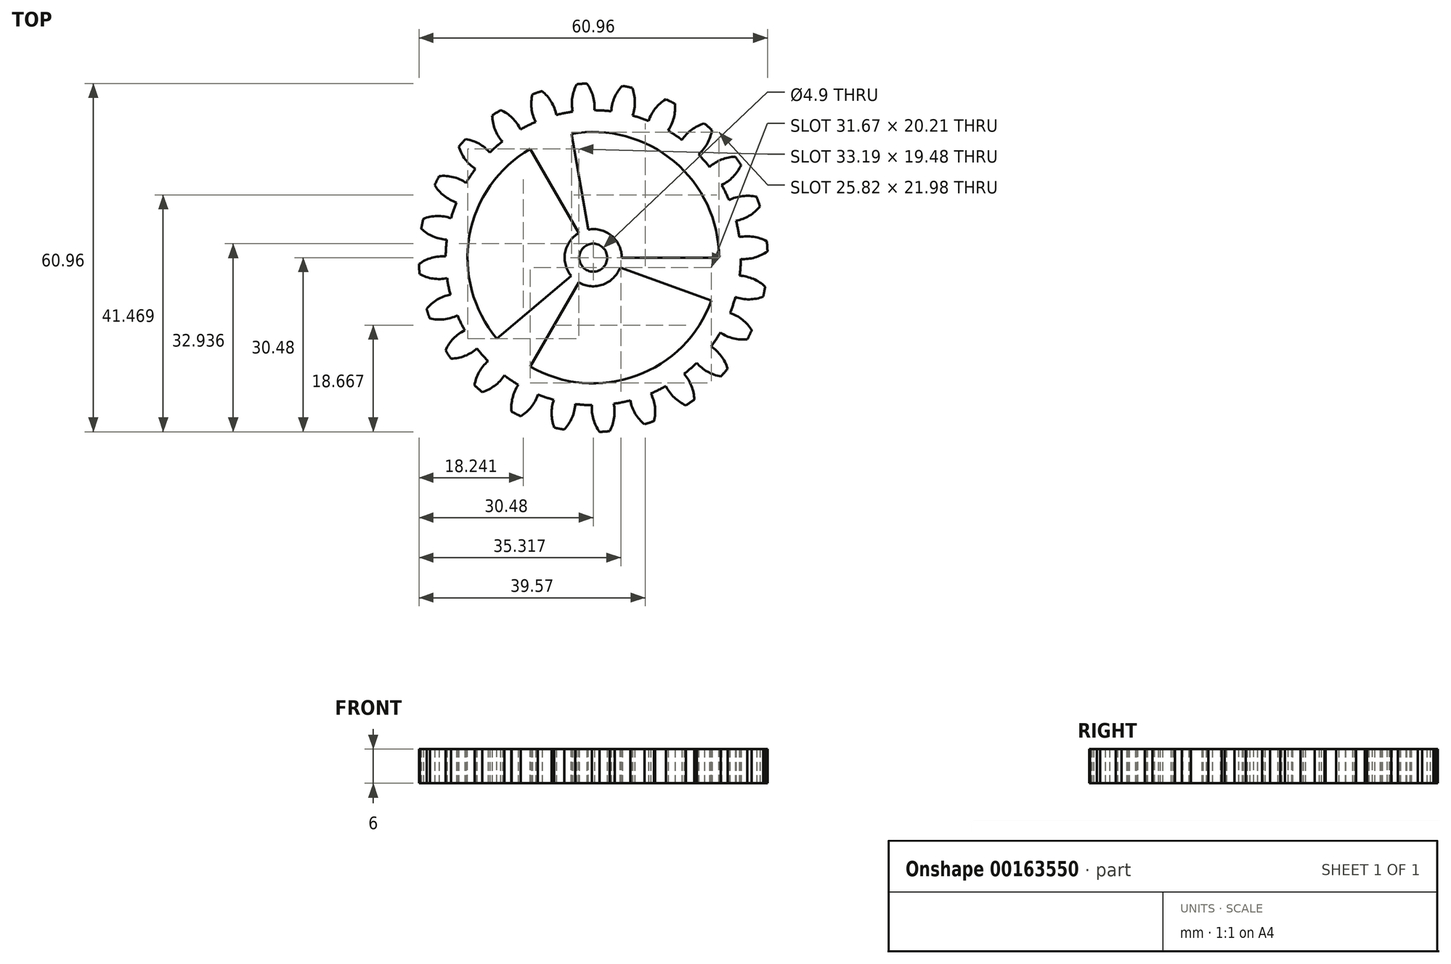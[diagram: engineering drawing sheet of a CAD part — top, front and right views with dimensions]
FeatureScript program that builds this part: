
annotation { "Feature Type Name" : "Feature", "Feature Type Description" : "" }
export const myFeature = defineFeature(function(context is Context, id is Id, definition is map)
    precondition{}
    {
        {
            var Q0;
            Q0=qCreatedBy(makeId("Top.planeOp"),FACE);
            var sketch = newSketch(context, id + "F0", { "sketchPlane" : qUnion([Q0])});
            skCircle(sketch, "E0", {"center": v(0, 0) * mm, "radius": 25.8 * mm, "construction": true});
            skCircle(sketch, "E1", {"center": v(0, 0) * mm, "radius": 28.15 * mm, "construction": true});
            skCircle(sketch, "E2", {"center": v(0, 0) * mm, "radius": 30.5 * mm, "construction": true});
            skLineSegment(sketch, "E3", {"start": v(0, 0) * mm, "end": v(0, 14.58) * mm, "construction": true});
            skLineSegment(sketch, "E4", {"start": v(0, 0) * mm, "end": v(-0.95, 14.56) * mm, "construction": true});
            skLineSegment(sketch, "E5", {"start": v(0, 28.15) * mm, "end": v(-10.54, 28.15) * mm, "construction": true});
            skLineSegment(sketch, "E6", {"start": v(0, 28.15) * mm, "end": v(-11.63, 25.04) * mm, "construction": true});
            skCircle(sketch, "E7", {"center": v(0, 28.15) * mm, "radius": 7.04 * mm, "construction": true});
            skCircle(sketch, "E8", {"center": v(-6.8, 26.33) * mm, "radius": 7.04 * mm, "construction": true});
            skArc(sketch, "E9", {"start": v(-13.6, 28.15) * mm, "mid": v(-13.7, 27.68) * mm, "end": v(-13.78, 27.2) * mm});
            skPoint(sketch, "E10.center", {"position": v(4.35, 4.65) * mm});
            skCircle(sketch, "E11", {"center": v(0, 0) * mm, "radius": 2.45 * mm});
            skArc(sketch, "E12", {"start": v(0.22, 25.8) * mm, "mid": v(-0.03, 28.26) * mm, "end": v(-1.11, 30.48) * mm});
            skArc(sketch, "E13.MirrorCS", {"start": v(-3.59, 25.56) * mm, "mid": v(-3.66, 28.02) * mm, "end": v(-2.88, 30.36) * mm});
            skArc(sketch, "E14", {"start": v(-1.11, 30.48) * mm, "mid": v(-2, 30.43) * mm, "end": v(-2.88, 30.36) * mm});
            skArc(sketch, "E15.1.0", {"start": v(-8.96, 29.15) * mm, "mid": v(-9.8, 28.88) * mm, "end": v(-10.64, 28.59) * mm});
            skArc(sketch, "E15.1.1", {"start": v(-6.47, 24.98) * mm, "mid": v(-7.34, 27.3) * mm, "end": v(-8.96, 29.15) * mm});
            skArc(sketch, "E15.1.2", {"start": v(-10.08, 23.76) * mm, "mid": v(-10.79, 26.12) * mm, "end": v(-10.64, 28.59) * mm});
            skArc(sketch, "E15.2.0", {"start": v(-16.2, 25.84) * mm, "mid": v(-16.94, 25.36) * mm, "end": v(-17.67, 24.86) * mm});
            skArc(sketch, "E15.2.1", {"start": v(-12.71, 22.46) * mm, "mid": v(-14.16, 24.46) * mm, "end": v(-16.2, 25.84) * mm});
            skArc(sketch, "E15.2.2", {"start": v(-15.88, 20.34) * mm, "mid": v(-17.18, 22.44) * mm, "end": v(-17.67, 24.86) * mm});
            skArc(sketch, "E15.3.0", {"start": v(-22.34, 20.77) * mm, "mid": v(-22.93, 20.11) * mm, "end": v(-23.5, 19.44) * mm});
            skArc(sketch, "E15.3.1", {"start": v(-18.1, 18.4) * mm, "mid": v(-20, 19.96) * mm, "end": v(-22.34, 20.77) * mm});
            skArc(sketch, "E15.3.2", {"start": v(-20.6, 15.54) * mm, "mid": v(-22.4, 17.23) * mm, "end": v(-23.5, 19.44) * mm});
            skArc(sketch, "E15.4.0", {"start": v(-26.95, 14.28) * mm, "mid": v(-27.35, 13.49) * mm, "end": v(-27.73, 12.7) * mm});
            skArc(sketch, "E15.4.1", {"start": v(-22.24, 13.1) * mm, "mid": v(-24.5, 14.1) * mm, "end": v(-26.95, 14.28) * mm});
            skArc(sketch, "E15.4.2", {"start": v(-23.93, 9.67) * mm, "mid": v(-26.1, 10.84) * mm, "end": v(-27.73, 12.7) * mm});
            skArc(sketch, "E15.5.0", {"start": v(-29.73, 6.81) * mm, "mid": v(-29.91, 5.95) * mm, "end": v(-30.07, 5.08) * mm});
            skArc(sketch, "E15.5.1", {"start": v(-24.87, 6.9) * mm, "mid": v(-27.3, 7.29) * mm, "end": v(-29.73, 6.81) * mm});
            skArc(sketch, "E15.5.2", {"start": v(-25.61, 3.15) * mm, "mid": v(-28.02, 3.72) * mm, "end": v(-30.07, 5.08) * mm});
            skArc(sketch, "E15.6.0", {"start": v(-30.48, -1.11) * mm, "mid": v(-30.43, -2) * mm, "end": v(-30.36, -2.88) * mm});
            skArc(sketch, "E15.6.1", {"start": v(-25.8, 0.22) * mm, "mid": v(-28.26, -0.03) * mm, "end": v(-30.48, -1.11) * mm});
            skArc(sketch, "E15.6.2", {"start": v(-25.56, -3.59) * mm, "mid": v(-28.02, -3.66) * mm, "end": v(-30.36, -2.88) * mm});
            skArc(sketch, "E15.7.0", {"start": v(-29.15, -8.96) * mm, "mid": v(-28.88, -9.8) * mm, "end": v(-28.59, -10.64) * mm});
            skArc(sketch, "E15.7.1", {"start": v(-24.98, -6.47) * mm, "mid": v(-27.3, -7.34) * mm, "end": v(-29.15, -8.96) * mm});
            skArc(sketch, "E15.7.2", {"start": v(-23.76, -10.08) * mm, "mid": v(-26.12, -10.79) * mm, "end": v(-28.59, -10.64) * mm});
            skArc(sketch, "E15.8.0", {"start": v(-25.84, -16.2) * mm, "mid": v(-25.36, -16.94) * mm, "end": v(-24.86, -17.67) * mm});
            skArc(sketch, "E15.8.1", {"start": v(-22.46, -12.71) * mm, "mid": v(-24.46, -14.16) * mm, "end": v(-25.84, -16.2) * mm});
            skArc(sketch, "E15.8.2", {"start": v(-20.34, -15.88) * mm, "mid": v(-22.44, -17.18) * mm, "end": v(-24.86, -17.67) * mm});
            skArc(sketch, "E15.9.0", {"start": v(-20.77, -22.34) * mm, "mid": v(-20.11, -22.93) * mm, "end": v(-19.44, -23.5) * mm});
            skArc(sketch, "E15.9.1", {"start": v(-18.4, -18.1) * mm, "mid": v(-19.96, -20) * mm, "end": v(-20.77, -22.34) * mm});
            skArc(sketch, "E15.9.2", {"start": v(-15.54, -20.6) * mm, "mid": v(-17.23, -22.4) * mm, "end": v(-19.44, -23.5) * mm});
            skArc(sketch, "E15.10.0", {"start": v(-14.28, -26.95) * mm, "mid": v(-13.49, -27.35) * mm, "end": v(-12.7, -27.73) * mm});
            skArc(sketch, "E15.10.1", {"start": v(-13.1, -22.24) * mm, "mid": v(-14.1, -24.5) * mm, "end": v(-14.28, -26.95) * mm});
            skArc(sketch, "E15.10.2", {"start": v(-9.67, -23.93) * mm, "mid": v(-10.84, -26.1) * mm, "end": v(-12.7, -27.73) * mm});
            skArc(sketch, "E15.11.0", {"start": v(-6.81, -29.73) * mm, "mid": v(-5.95, -29.91) * mm, "end": v(-5.08, -30.07) * mm});
            skArc(sketch, "E15.11.1", {"start": v(-6.9, -24.87) * mm, "mid": v(-7.29, -27.3) * mm, "end": v(-6.81, -29.73) * mm});
            skArc(sketch, "E15.11.2", {"start": v(-3.15, -25.61) * mm, "mid": v(-3.72, -28.02) * mm, "end": v(-5.08, -30.07) * mm});
            skArc(sketch, "E15.12.0", {"start": v(1.11, -30.48) * mm, "mid": v(2, -30.43) * mm, "end": v(2.88, -30.36) * mm});
            skArc(sketch, "E15.12.1", {"start": v(-0.22, -25.8) * mm, "mid": v(0.03, -28.26) * mm, "end": v(1.11, -30.48) * mm});
            skArc(sketch, "E15.12.2", {"start": v(3.59, -25.56) * mm, "mid": v(3.66, -28.02) * mm, "end": v(2.88, -30.36) * mm});
            skArc(sketch, "E15.13.0", {"start": v(8.96, -29.15) * mm, "mid": v(9.8, -28.88) * mm, "end": v(10.64, -28.59) * mm});
            skArc(sketch, "E15.13.1", {"start": v(6.47, -24.98) * mm, "mid": v(7.34, -27.3) * mm, "end": v(8.96, -29.15) * mm});
            skArc(sketch, "E15.13.2", {"start": v(10.08, -23.76) * mm, "mid": v(10.79, -26.12) * mm, "end": v(10.64, -28.59) * mm});
            skArc(sketch, "E15.14.0", {"start": v(16.2, -25.84) * mm, "mid": v(16.94, -25.36) * mm, "end": v(17.67, -24.86) * mm});
            skArc(sketch, "E15.14.1", {"start": v(12.71, -22.46) * mm, "mid": v(14.16, -24.46) * mm, "end": v(16.2, -25.84) * mm});
            skArc(sketch, "E15.14.2", {"start": v(15.88, -20.34) * mm, "mid": v(17.18, -22.44) * mm, "end": v(17.67, -24.86) * mm});
            skArc(sketch, "E15.15.0", {"start": v(22.34, -20.77) * mm, "mid": v(22.93, -20.11) * mm, "end": v(23.5, -19.44) * mm});
            skArc(sketch, "E15.15.1", {"start": v(18.1, -18.4) * mm, "mid": v(20, -19.96) * mm, "end": v(22.34, -20.77) * mm});
            skArc(sketch, "E15.15.2", {"start": v(20.6, -15.54) * mm, "mid": v(22.4, -17.23) * mm, "end": v(23.5, -19.44) * mm});
            skArc(sketch, "E15.16.0", {"start": v(26.95, -14.28) * mm, "mid": v(27.35, -13.49) * mm, "end": v(27.73, -12.7) * mm});
            skArc(sketch, "E15.16.1", {"start": v(22.24, -13.1) * mm, "mid": v(24.5, -14.1) * mm, "end": v(26.95, -14.28) * mm});
            skArc(sketch, "E15.16.2", {"start": v(23.93, -9.67) * mm, "mid": v(26.1, -10.84) * mm, "end": v(27.73, -12.7) * mm});
            skArc(sketch, "E15.17.0", {"start": v(29.73, -6.81) * mm, "mid": v(29.91, -5.95) * mm, "end": v(30.07, -5.08) * mm});
            skArc(sketch, "E15.17.1", {"start": v(24.87, -6.9) * mm, "mid": v(27.3, -7.29) * mm, "end": v(29.73, -6.81) * mm});
            skArc(sketch, "E15.17.2", {"start": v(25.61, -3.15) * mm, "mid": v(28.02, -3.72) * mm, "end": v(30.07, -5.08) * mm});
            skArc(sketch, "E15.18.0", {"start": v(30.48, 1.11) * mm, "mid": v(30.43, 2) * mm, "end": v(30.36, 2.88) * mm});
            skArc(sketch, "E15.18.1", {"start": v(25.8, -0.22) * mm, "mid": v(28.26, 0.03) * mm, "end": v(30.48, 1.11) * mm});
            skArc(sketch, "E15.18.2", {"start": v(25.56, 3.59) * mm, "mid": v(28.02, 3.66) * mm, "end": v(30.36, 2.88) * mm});
            skArc(sketch, "E15.19.0", {"start": v(29.15, 8.96) * mm, "mid": v(28.88, 9.8) * mm, "end": v(28.59, 10.64) * mm});
            skArc(sketch, "E15.19.1", {"start": v(24.98, 6.47) * mm, "mid": v(27.3, 7.34) * mm, "end": v(29.15, 8.96) * mm});
            skArc(sketch, "E15.19.2", {"start": v(23.76, 10.08) * mm, "mid": v(26.12, 10.79) * mm, "end": v(28.59, 10.64) * mm});
            skArc(sketch, "E15.20.0", {"start": v(25.84, 16.2) * mm, "mid": v(25.36, 16.94) * mm, "end": v(24.86, 17.67) * mm});
            skArc(sketch, "E15.20.1", {"start": v(22.46, 12.71) * mm, "mid": v(24.46, 14.16) * mm, "end": v(25.84, 16.2) * mm});
            skArc(sketch, "E15.20.2", {"start": v(20.34, 15.88) * mm, "mid": v(22.44, 17.18) * mm, "end": v(24.86, 17.67) * mm});
            skArc(sketch, "E15.21.0", {"start": v(20.77, 22.34) * mm, "mid": v(20.11, 22.93) * mm, "end": v(19.44, 23.5) * mm});
            skArc(sketch, "E15.21.1", {"start": v(18.4, 18.1) * mm, "mid": v(19.96, 20) * mm, "end": v(20.77, 22.34) * mm});
            skArc(sketch, "E15.21.2", {"start": v(15.54, 20.6) * mm, "mid": v(17.23, 22.4) * mm, "end": v(19.44, 23.5) * mm});
            skArc(sketch, "E15.22.0", {"start": v(14.28, 26.95) * mm, "mid": v(13.49, 27.35) * mm, "end": v(12.7, 27.73) * mm});
            skArc(sketch, "E15.22.1", {"start": v(13.1, 22.24) * mm, "mid": v(14.1, 24.5) * mm, "end": v(14.28, 26.95) * mm});
            skArc(sketch, "E15.22.2", {"start": v(9.67, 23.93) * mm, "mid": v(10.84, 26.1) * mm, "end": v(12.7, 27.73) * mm});
            skArc(sketch, "E15.23.0", {"start": v(6.81, 29.73) * mm, "mid": v(5.95, 29.91) * mm, "end": v(5.08, 30.07) * mm});
            skArc(sketch, "E15.23.1", {"start": v(6.9, 24.87) * mm, "mid": v(7.29, 27.3) * mm, "end": v(6.81, 29.73) * mm});
            skArc(sketch, "E15.23.2", {"start": v(3.15, 25.61) * mm, "mid": v(3.72, 28.02) * mm, "end": v(5.08, 30.07) * mm});
            skArc(sketch, "E16", {"start": v(3.15, 25.61) * mm, "mid": v(1.69, 25.75) * mm, "end": v(0.22, 25.8) * mm});
            skArc(sketch, "E17.1.0", {"start": v(-3.59, 25.56) * mm, "mid": v(-5.03, 25.31) * mm, "end": v(-6.47, 24.98) * mm});
            skArc(sketch, "E17.2.0", {"start": v(-10.08, 23.76) * mm, "mid": v(-11.41, 23.15) * mm, "end": v(-12.71, 22.46) * mm});
            skArc(sketch, "E17.3.0", {"start": v(-15.88, 20.34) * mm, "mid": v(-17.02, 19.4) * mm, "end": v(-18.1, 18.4) * mm});
            skArc(sketch, "E17.4.0", {"start": v(-20.6, 15.54) * mm, "mid": v(-21.46, 14.34) * mm, "end": v(-22.24, 13.1) * mm});
            skArc(sketch, "E17.5.0", {"start": v(-23.93, 9.67) * mm, "mid": v(-24.44, 8.3) * mm, "end": v(-24.87, 6.9) * mm});
            skArc(sketch, "E17.6.0", {"start": v(-25.61, 3.15) * mm, "mid": v(-25.75, 1.69) * mm, "end": v(-25.8, 0.22) * mm});
            skArc(sketch, "E17.7.0", {"start": v(-25.56, -3.59) * mm, "mid": v(-25.31, -5.03) * mm, "end": v(-24.98, -6.47) * mm});
            skArc(sketch, "E17.8.0", {"start": v(-23.76, -10.08) * mm, "mid": v(-23.15, -11.41) * mm, "end": v(-22.46, -12.71) * mm});
            skArc(sketch, "E17.9.0", {"start": v(-20.34, -15.88) * mm, "mid": v(-19.4, -17.02) * mm, "end": v(-18.4, -18.1) * mm});
            skArc(sketch, "E17.10.0", {"start": v(-15.54, -20.6) * mm, "mid": v(-14.34, -21.46) * mm, "end": v(-13.1, -22.24) * mm});
            skArc(sketch, "E17.11.0", {"start": v(-9.67, -23.93) * mm, "mid": v(-8.3, -24.44) * mm, "end": v(-6.9, -24.87) * mm});
            skArc(sketch, "E17.12.0", {"start": v(-3.15, -25.61) * mm, "mid": v(-1.69, -25.75) * mm, "end": v(-0.22, -25.8) * mm});
            skArc(sketch, "E17.13.0", {"start": v(3.59, -25.56) * mm, "mid": v(5.03, -25.31) * mm, "end": v(6.47, -24.98) * mm});
            skArc(sketch, "E17.14.0", {"start": v(10.08, -23.76) * mm, "mid": v(11.41, -23.15) * mm, "end": v(12.71, -22.46) * mm});
            skArc(sketch, "E17.15.0", {"start": v(15.88, -20.34) * mm, "mid": v(17.02, -19.4) * mm, "end": v(18.1, -18.4) * mm});
            skArc(sketch, "E17.16.0", {"start": v(20.6, -15.54) * mm, "mid": v(21.46, -14.34) * mm, "end": v(22.24, -13.1) * mm});
            skArc(sketch, "E17.17.0", {"start": v(23.93, -9.67) * mm, "mid": v(24.44, -8.3) * mm, "end": v(24.87, -6.9) * mm});
            skArc(sketch, "E17.18.0", {"start": v(25.61, -3.15) * mm, "mid": v(25.75, -1.69) * mm, "end": v(25.8, -0.22) * mm});
            skArc(sketch, "E17.19.0", {"start": v(25.56, 3.59) * mm, "mid": v(25.31, 5.03) * mm, "end": v(24.98, 6.47) * mm});
            skArc(sketch, "E17.20.0", {"start": v(23.76, 10.08) * mm, "mid": v(23.15, 11.41) * mm, "end": v(22.46, 12.71) * mm});
            skArc(sketch, "E17.21.0", {"start": v(20.34, 15.88) * mm, "mid": v(19.4, 17.02) * mm, "end": v(18.4, 18.1) * mm});
            skArc(sketch, "E17.22.0", {"start": v(15.54, 20.6) * mm, "mid": v(14.34, 21.46) * mm, "end": v(13.1, 22.24) * mm});
            skArc(sketch, "E17.23.0", {"start": v(9.67, 23.93) * mm, "mid": v(8.3, 24.44) * mm, "end": v(6.9, 24.87) * mm});
            skSolve(sketch);
        }
        {
            var Q0;
            Q0=makeQuery(id+"F0.imprint","IMPRINT",FACE,{"disambiguationData":[TD([[makeQuery(id+"F0.imprint","IMPRINT",EDGE,{"derivedFrom":sQuery(id+"F0.wireOp",EDGE,"E11")}),-1.0]])]});
            extrude(context, id + "F1", {"entities" : qUnion([Q0]), "depth" : 6 * mm});
        }
        {
            var Q0;
            Q0=makeQuery(id+"F1.opExtrude","CAP_FACE",FACE,{"disambiguationData":[OSD([sQuery(id+"F0.wireOp",EDGE,"E11"),sQuery(id+"F0.wireOp",EDGE,"E12"),sQuery(id+"F0.wireOp",EDGE,"E13.MirrorCS"),sQuery(id+"F0.wireOp",EDGE,"E14"),sQuery(id+"F0.wireOp",EDGE,"E15.1.0"),sQuery(id+"F0.wireOp",EDGE,"E15.1.1"),sQuery(id+"F0.wireOp",EDGE,"E15.1.2"),sQuery(id+"F0.wireOp",EDGE,"E15.2.0"),sQuery(id+"F0.wireOp",EDGE,"E15.2.1"),sQuery(id+"F0.wireOp",EDGE,"E15.2.2"),sQuery(id+"F0.wireOp",EDGE,"E15.3.0"),sQuery(id+"F0.wireOp",EDGE,"E15.3.1"),sQuery(id+"F0.wireOp",EDGE,"E15.3.2"),sQuery(id+"F0.wireOp",EDGE,"E15.4.0"),sQuery(id+"F0.wireOp",EDGE,"E15.4.1"),sQuery(id+"F0.wireOp",EDGE,"E15.4.2"),sQuery(id+"F0.wireOp",EDGE,"E15.5.0"),sQuery(id+"F0.wireOp",EDGE,"E15.5.1"),sQuery(id+"F0.wireOp",EDGE,"E15.5.2"),sQuery(id+"F0.wireOp",EDGE,"E15.6.0"),sQuery(id+"F0.wireOp",EDGE,"E15.6.1"),sQuery(id+"F0.wireOp",EDGE,"E15.6.2"),sQuery(id+"F0.wireOp",EDGE,"E15.7.0"),sQuery(id+"F0.wireOp",EDGE,"E15.7.1"),sQuery(id+"F0.wireOp",EDGE,"E15.7.2"),sQuery(id+"F0.wireOp",EDGE,"E15.8.0"),sQuery(id+"F0.wireOp",EDGE,"E15.8.1"),sQuery(id+"F0.wireOp",EDGE,"E15.8.2"),sQuery(id+"F0.wireOp",EDGE,"E15.9.0"),sQuery(id+"F0.wireOp",EDGE,"E15.9.1"),sQuery(id+"F0.wireOp",EDGE,"E15.9.2"),sQuery(id+"F0.wireOp",EDGE,"E15.10.0"),sQuery(id+"F0.wireOp",EDGE,"E15.10.1"),sQuery(id+"F0.wireOp",EDGE,"E15.10.2"),sQuery(id+"F0.wireOp",EDGE,"E15.11.0"),sQuery(id+"F0.wireOp",EDGE,"E15.11.1"),sQuery(id+"F0.wireOp",EDGE,"E15.11.2"),sQuery(id+"F0.wireOp",EDGE,"E15.12.0"),sQuery(id+"F0.wireOp",EDGE,"E15.12.1"),sQuery(id+"F0.wireOp",EDGE,"E15.12.2"),sQuery(id+"F0.wireOp",EDGE,"E15.13.0"),sQuery(id+"F0.wireOp",EDGE,"E15.13.1"),sQuery(id+"F0.wireOp",EDGE,"E15.13.2"),sQuery(id+"F0.wireOp",EDGE,"E15.14.0"),sQuery(id+"F0.wireOp",EDGE,"E15.14.1"),sQuery(id+"F0.wireOp",EDGE,"E15.14.2"),sQuery(id+"F0.wireOp",EDGE,"E15.15.0"),sQuery(id+"F0.wireOp",EDGE,"E15.15.1"),sQuery(id+"F0.wireOp",EDGE,"E15.15.2"),sQuery(id+"F0.wireOp",EDGE,"E15.16.0"),sQuery(id+"F0.wireOp",EDGE,"E15.16.1"),sQuery(id+"F0.wireOp",EDGE,"E15.16.2"),sQuery(id+"F0.wireOp",EDGE,"E15.17.0"),sQuery(id+"F0.wireOp",EDGE,"E15.17.1"),sQuery(id+"F0.wireOp",EDGE,"E15.17.2"),sQuery(id+"F0.wireOp",EDGE,"E15.18.0"),sQuery(id+"F0.wireOp",EDGE,"E15.18.1"),sQuery(id+"F0.wireOp",EDGE,"E15.18.2"),sQuery(id+"F0.wireOp",EDGE,"E15.19.0"),sQuery(id+"F0.wireOp",EDGE,"E15.19.1"),sQuery(id+"F0.wireOp",EDGE,"E15.19.2"),sQuery(id+"F0.wireOp",EDGE,"E15.20.0"),sQuery(id+"F0.wireOp",EDGE,"E15.20.1"),sQuery(id+"F0.wireOp",EDGE,"E15.20.2"),sQuery(id+"F0.wireOp",EDGE,"E15.21.0"),sQuery(id+"F0.wireOp",EDGE,"E15.21.1"),sQuery(id+"F0.wireOp",EDGE,"E15.21.2"),sQuery(id+"F0.wireOp",EDGE,"E15.22.0"),sQuery(id+"F0.wireOp",EDGE,"E15.22.1"),sQuery(id+"F0.wireOp",EDGE,"E15.22.2"),sQuery(id+"F0.wireOp",EDGE,"E15.23.0"),sQuery(id+"F0.wireOp",EDGE,"E15.23.1"),sQuery(id+"F0.wireOp",EDGE,"E15.23.2"),sQuery(id+"F0.wireOp",EDGE,"E16"),sQuery(id+"F0.wireOp",EDGE,"E17.1.0"),sQuery(id+"F0.wireOp",EDGE,"E17.2.0"),sQuery(id+"F0.wireOp",EDGE,"E17.3.0"),sQuery(id+"F0.wireOp",EDGE,"E17.4.0"),sQuery(id+"F0.wireOp",EDGE,"E17.5.0"),sQuery(id+"F0.wireOp",EDGE,"E17.6.0"),sQuery(id+"F0.wireOp",EDGE,"E17.7.0"),sQuery(id+"F0.wireOp",EDGE,"E17.8.0"),sQuery(id+"F0.wireOp",EDGE,"E17.9.0"),sQuery(id+"F0.wireOp",EDGE,"E17.10.0"),sQuery(id+"F0.wireOp",EDGE,"E17.11.0"),sQuery(id+"F0.wireOp",EDGE,"E17.12.0"),sQuery(id+"F0.wireOp",EDGE,"E17.13.0"),sQuery(id+"F0.wireOp",EDGE,"E17.14.0"),sQuery(id+"F0.wireOp",EDGE,"E17.15.0"),sQuery(id+"F0.wireOp",EDGE,"E17.16.0"),sQuery(id+"F0.wireOp",EDGE,"E17.17.0"),sQuery(id+"F0.wireOp",EDGE,"E17.18.0"),sQuery(id+"F0.wireOp",EDGE,"E17.19.0"),sQuery(id+"F0.wireOp",EDGE,"E17.20.0"),sQuery(id+"F0.wireOp",EDGE,"E17.21.0"),sQuery(id+"F0.wireOp",EDGE,"E17.22.0"),sQuery(id+"F0.wireOp",EDGE,"E17.23.0")])],"isStart":false});
            var sketch = newSketch(context, id + "F2", { "sketchPlane" : qUnion([Q0])});
            skCircle(sketch, "E18", {"center": v(0, 0) * mm, "radius": 5 * mm});
            skLineSegment(sketch, "E19", {"start": v(0, 0) * mm, "end": v(5, 0) * mm, "construction": true});
            skLineSegment(sketch, "E20", {"start": v(0, 0) * mm, "end": v(-0.87, 4.92) * mm, "construction": true});
            skLineSegment(sketch, "E21", {"start": v(5, 0) * mm, "end": v(22, 0) * mm});
            skLineSegment(sketch, "E22", {"start": v(-0.87, 4.92) * mm, "end": v(-3.82, 21.67) * mm});
            skArc(sketch, "E23", {"start": v(22, 0) * mm, "mid": v(14.14, 16.85) * mm, "end": v(-3.82, 21.67) * mm});
            skArc(sketch, "E24.1.0", {"start": v(-11, 19.05) * mm, "mid": v(-21.67, 3.82) * mm, "end": v(-16.85, -14.14) * mm});
            skLineSegment(sketch, "E24.1.1", {"start": v(-2.5, 4.33) * mm, "end": v(-11, 19.05) * mm});
            skLineSegment(sketch, "E24.1.2", {"start": v(-3.83, -3.21) * mm, "end": v(-16.85, -14.14) * mm});
            skArc(sketch, "E24.2.0", {"start": v(-11, -19.05) * mm, "mid": v(7.52, -20.67) * mm, "end": v(20.67, -7.52) * mm});
            skLineSegment(sketch, "E24.2.1", {"start": v(-2.5, -4.33) * mm, "end": v(-11, -19.05) * mm});
            skLineSegment(sketch, "E24.2.2", {"start": v(4.7, -1.71) * mm, "end": v(20.67, -7.52) * mm});
            skSolve(sketch);
        }
        {
            var Q0;
            Q0=makeQuery(id+"F2.imprint","IMPRINT",FACE,{"disambiguationData":[TD([[makeQuery(id+"F2.imprint","IMPRINT",EDGE,{"derivedFrom":sQuery(id+"F2.wireOp",EDGE,"E24.2.0")}),1.0]])]});
            var Q1;
            {var subQ0=sQuery(id+"F2.wireOp",EDGE,"E21");Q1=makeQuery(id+"F2.imprint","IMPRINT",FACE,{"disambiguationData":[TD([[makeQuery(id+"F2.imprint","IMPRINT",EDGE,{"derivedFrom":subQ0}),1.0]])]});}
            var Q2;
            Q2=makeQuery(id+"F2.imprint","IMPRINT",FACE,{"disambiguationData":[TD([[makeQuery(id+"F2.imprint","IMPRINT",EDGE,{"derivedFrom":sQuery(id+"F2.wireOp",EDGE,"E24.1.0")}),1.0]])]});
            extrude(context, id + "F3", {"entities" : qUnion([Q0, Q1, Q2]), "operationType" : NewBodyOperationType.REMOVE, "oppositeDirection" : true, "depth" : 25 * mm});
        }
    });
